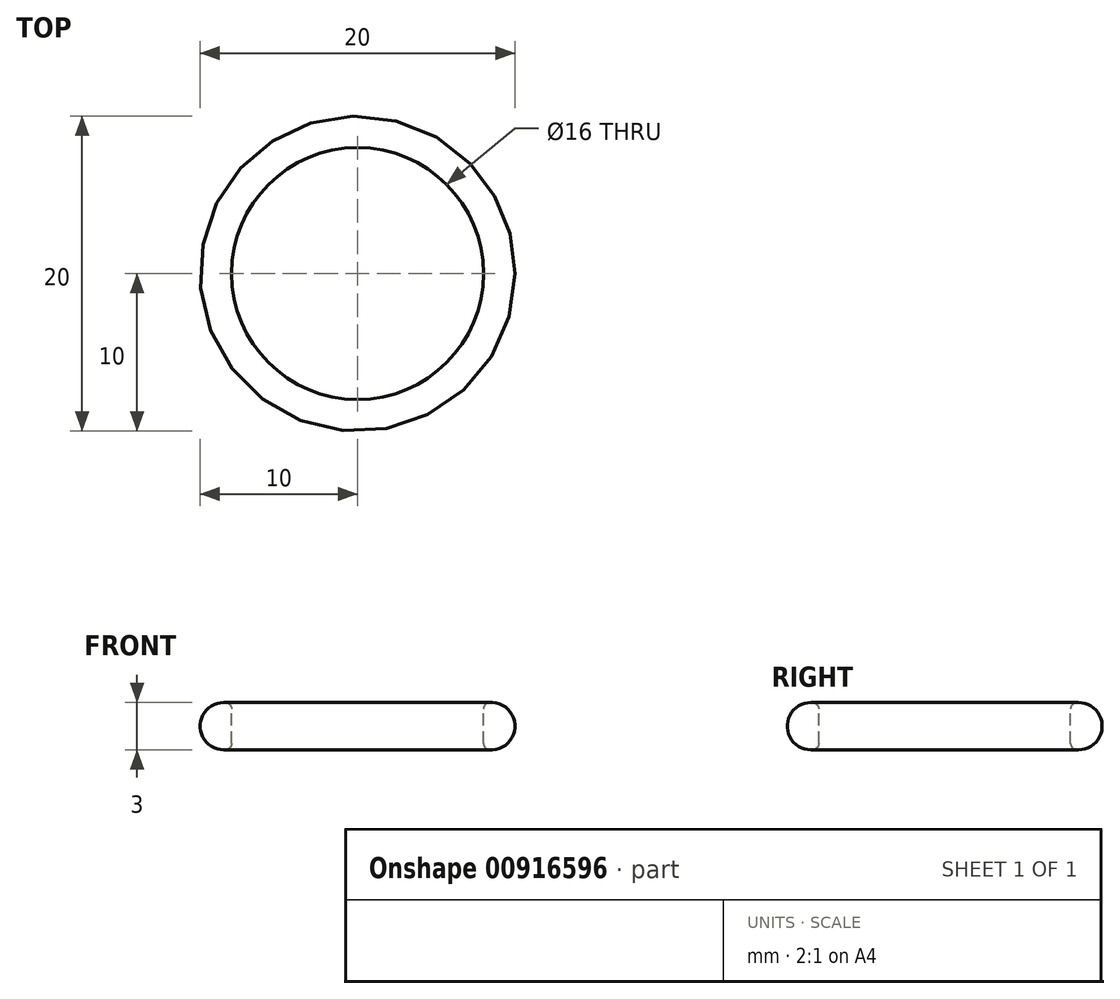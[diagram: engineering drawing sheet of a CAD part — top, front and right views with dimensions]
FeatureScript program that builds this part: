
annotation { "Feature Type Name" : "Feature", "Feature Type Description" : "" }
export const myFeature = defineFeature(function(context is Context, id is Id, definition is map)
    precondition{}
    {
        {
            var Q0;
            Q0=qCreatedBy(makeId("Front.planeOp"),FACE);
            var sketch = newSketch(context, id + "F0", { "sketchPlane" : qUnion([Q0])});
            skArc(sketch, "E0", {"start": v(0.14, 1.5) * mm, "mid": v(-1.5, 0) * mm, "end": v(0.14, -1.5) * mm});
            skLineSegment(sketch, "E1", {"start": v(0.5, 1.1) * mm, "end": v(0.5, -1.1) * mm});
            skPoint(sketch, "E2.visualSharp", {"position": v(0.5, 1.41) * mm});
            skArc(sketch, "E2.filletArc", {"start": v(0.5, 1.1) * mm, "mid": v(0.4, 1.37) * mm, "end": v(0.14, 1.5) * mm});
            skPoint(sketch, "E3.visualSharp", {"position": v(0.5, -1.41) * mm});
            skArc(sketch, "E3.filletArc", {"start": v(0.14, -1.5) * mm, "mid": v(0.4, -1.37) * mm, "end": v(0.5, -1.1) * mm});
            skLineSegment(sketch, "E4", {"start": v(8.5, 2.01) * mm, "end": v(8.5, -5.14) * mm});
            skSolve(sketch);
        }
        {
            var Q0;
            Q0 = qSketchRegion(id + "F0", true);
            var Q1;
            Q1=sQuery(id+"F0.wireOp",EDGE,"E4");
            revolve(context, id + "F1", {"surfaceOperationType" : NewSurfaceOperationType.NEW, "entities" : qUnion([Q0]), "axis" : qUnion([Q1]), "revolveType" : RevolveType.FULL});
        }
    });
